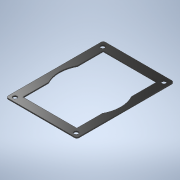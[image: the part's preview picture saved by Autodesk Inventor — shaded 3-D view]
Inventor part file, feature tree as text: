
AUTODESK INVENTOR PART (.ipt)
format: ipt  version: 2020.3 (Build 243373000, 373)  size: 129,536 bytes
history: native  units: mm
features: extrude x1, sketch x1
ambient origin geometry x8: Origin, YZ Plane, XZ Plane, XY Plane, X Axis, Y Axis, Z Axis, Center Point
bodies: Body1 (feature_tree)
feature tree (2):
  extrude  "Extrusion9"  Depth=92.0mm
  sketch  "Sketch1"  dims[d40=67.0mm d41=92.0mm d42=2.0mm d43=51.0mm d44=76.0mm d47=1.0mm d48=0.0mm d8=0.5mm d9=0.872665mm d10=0.5mm d11=0.872665mm]
